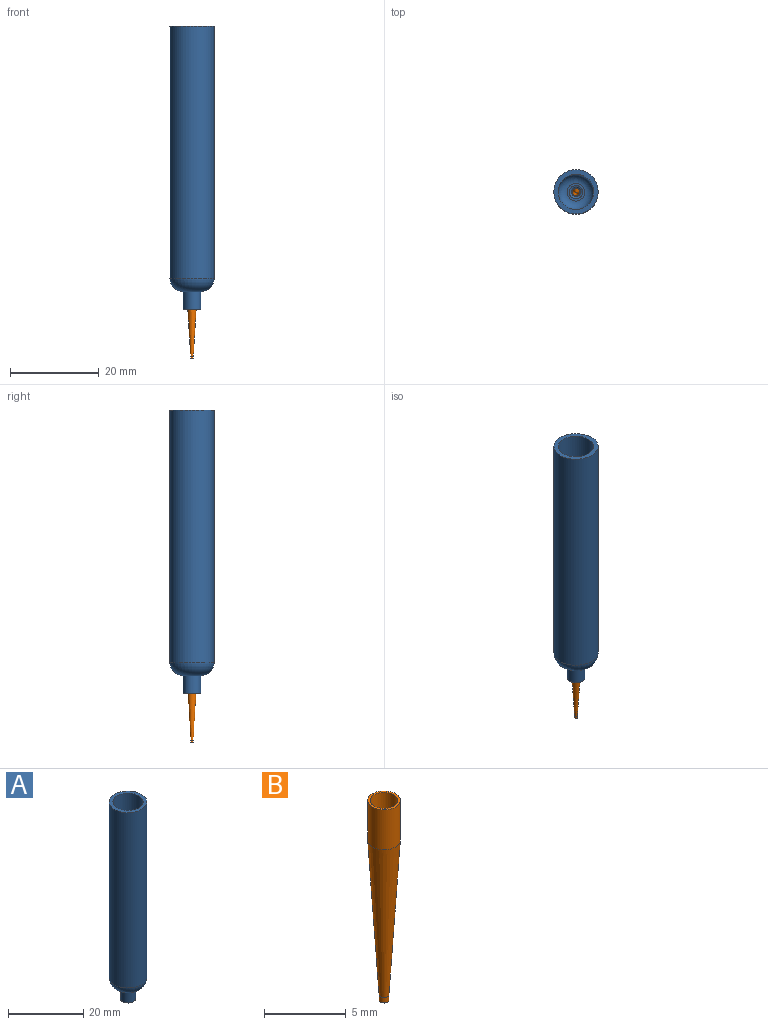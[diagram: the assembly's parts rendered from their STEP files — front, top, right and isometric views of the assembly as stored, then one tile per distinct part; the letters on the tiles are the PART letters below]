
ASSEMBLY  parts=2 mates=1
PART A: 10 faces, bbox 10x10x64 mm
  f0: torus R=2mm, axis (0,0,1), area 115.8mm2, adj f1,f9
  f1: cylinder r=2mm len=4mm, axis (0,0,1), area 50.3mm2, adj f0,f2
  f2: plane 4x4mm, normal (0,0,-1), area 9.4mm2, adj f1,f3
  f3: cylinder r=1mm len=4.5mm, axis (0,0,1), area 28.3mm2, adj f2,f4
  f4: torus R=1.5mm, axis (0,0,1), area 5.8mm2, adj f3,f5
  f5: plane 4x4mm, normal (0,0,1), area 5.5mm2, adj f4,f6
  f6: torus R=2mm, axis (0,0,1), area 64.6mm2, adj f5,f7
  f7: cylinder r=4mm len=57mm, axis (0,0,1), area 1432.6mm2, adj f6,f8
  f8: plane 10x10mm, normal (0,0,1), area 28.3mm2, adj f7,f9
  f9: cylinder r=5mm len=57mm, axis (0,0,1), area 1790.7mm2, adj f0,f8
PART B: 8 faces, bbox 2x2x15 mm
  f0: cone r=0.3mm half-angle=3.5deg, axis (0,0,1), area 47.5mm2, adj f1,f7
  f1: cylinder r=0.3mm len=0.6mm, axis (0,0,1), area 0.8mm2, adj f0,f2
  f2: plane 0.6x0.6mm, normal (0,0,-1), area 0.2mm2, adj f1,f3
  f3: cylinder r=0.15mm len=0.4mm, axis (0,0,1), area 0.4mm2, adj f2,f4
  f4: cone r=0.15mm half-angle=3.5deg, axis (0,0,1), area 36.5mm2, adj f3,f5
  f5: cylinder r=0.85mm len=3mm, axis (0,0,1), area 16mm2, adj f4,f6
  f6: plane 2x2mm, normal (0,0,1), area 0.9mm2, adj f5,f7
  f7: cylinder r=1mm len=3mm, axis (0,0,1), area 18.8mm2, adj f0,f6
PLACE A t=(-21.13,34.4,20.77)mm
PLACE B t=(-21.13,34.4,-16.73)mm
MATE fastened A.f1 <-> B.f0  axis (0,0,1) through (-21.13,34.4,-9.23)mm
